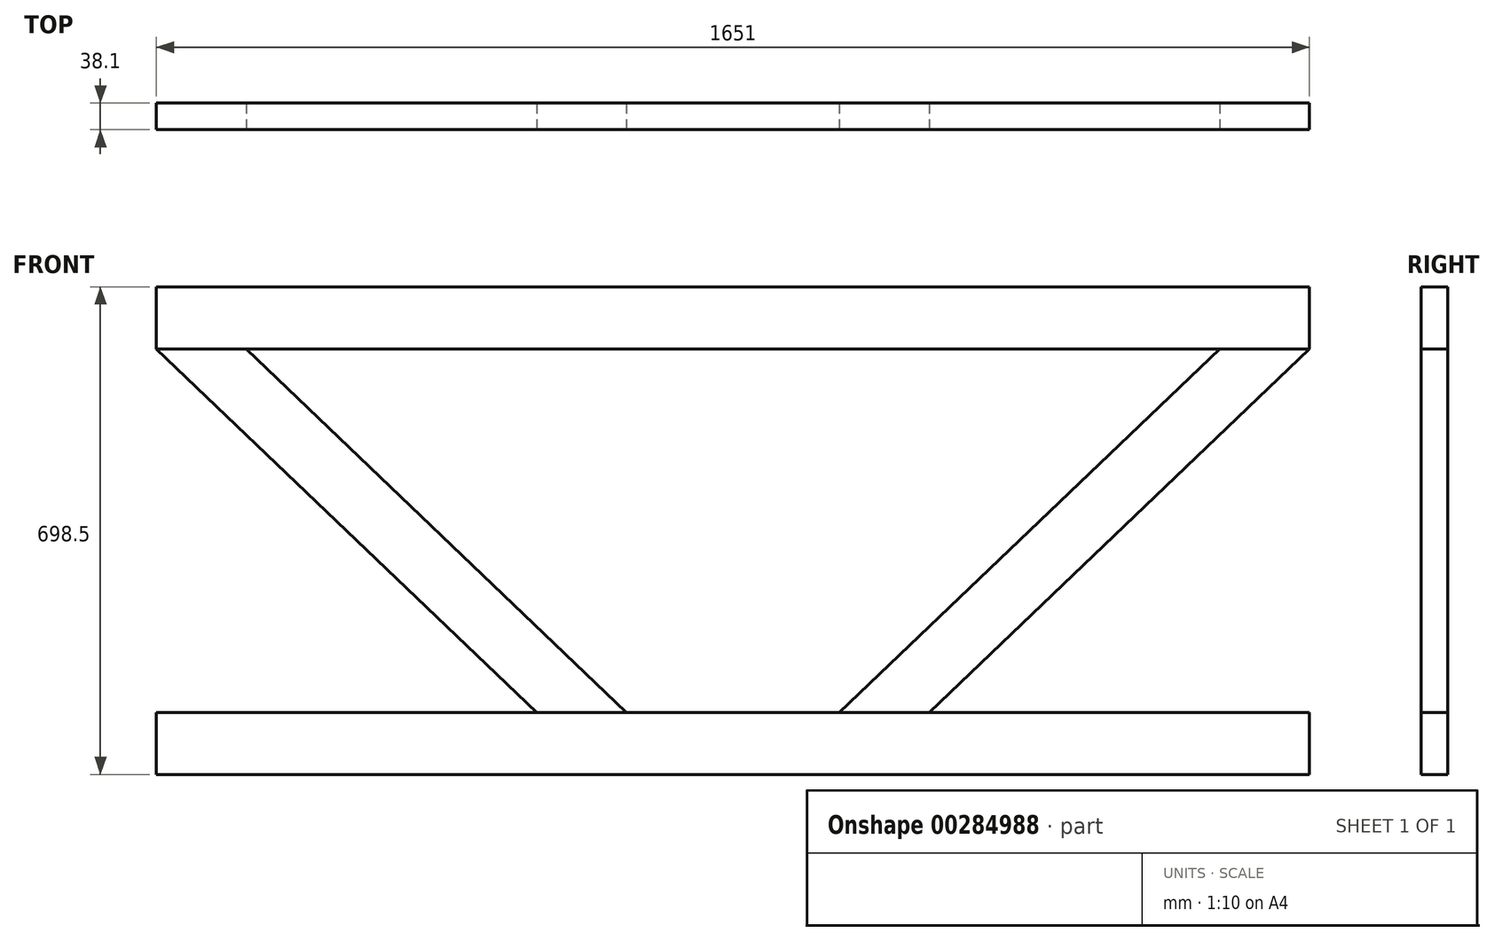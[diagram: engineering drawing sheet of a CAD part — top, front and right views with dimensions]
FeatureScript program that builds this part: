
annotation { "Feature Type Name" : "Feature", "Feature Type Description" : "" }
export const myFeature = defineFeature(function(context is Context, id is Id, definition is map)
    precondition{}
    {
        {
            var Q0;
            Q0=qCreatedBy(makeId("Front.planeOp"),FACE);
            var sketch = newSketch(context, id + "F0", { "sketchPlane" : qUnion([Q0])});
            skLineSegment(sketch, "E0.bottom", {"start": v(0, 0) * mm, "end": v(1651, 0) * mm});
            skLineSegment(sketch, "E0.top", {"start": v(0, 88.9) * mm, "end": v(1651, 88.9) * mm});
            skLineSegment(sketch, "E0.left", {"start": v(0, 0) * mm, "end": v(0, 88.9) * mm});
            skLineSegment(sketch, "E0.right", {"start": v(1651, 0) * mm, "end": v(1651, 88.9) * mm});
            skSolve(sketch);
        }
        {
            var Q0;
            Q0=makeQuery(id+"F0.imprint","IMPRINT",FACE,{"disambiguationData":[TD([[makeQuery(id+"F0.imprint","IMPRINT",EDGE,{"derivedFrom":sQuery(id+"F0.wireOp",EDGE,"E0.bottom")}),1.0]])]});
            extrude(context, id + "F1", {"entities" : qUnion([Q0]), "endBound" : BoundingType.SYMMETRIC, "depth" : 38.1 * mm});
        }
        {
            var Q0;
            Q0=qCreatedBy(makeId("Top.planeOp"),FACE);
            cPlane(context, id + "F2", {"entities" : qUnion([Q0]), "cplaneType" : CPlaneType.OFFSET, "offset" : 349.25 * mm, "width" : 152.4 * mm, "height" : 152.4 * mm});
        }
        {
            var Q0;
            Q0=makeQuery(id+"F1.opExtrude","SWEPT_BODY",BODY,{"disambiguationData":[OSD([sQuery(id+"F0.wireOp",EDGE,"E0.bottom"),sQuery(id+"F0.wireOp",EDGE,"E0.top"),sQuery(id+"F0.wireOp",EDGE,"E0.left"),sQuery(id+"F0.wireOp",EDGE,"E0.right")])]});
            var Q1;
            Q1=qCreatedBy(id+"F2.planeOp",FACE);
            mirror(context, id + "F3", {"entities" : qUnion([Q0]), "mirrorPlane" : qUnion([Q1])});
        }
        {
            var Q0;
            Q0=makeQuery(id+"F3.opPattern","COPY",FACE,{"derivedFrom":makeQuery(id+"F1.opExtrude","CAP_FACE",FACE,{"disambiguationData":[OSD([sQuery(id+"F0.wireOp",EDGE,"E0.bottom"),sQuery(id+"F0.wireOp",EDGE,"E0.top"),sQuery(id+"F0.wireOp",EDGE,"E0.left"),sQuery(id+"F0.wireOp",EDGE,"E0.right")])],"isStart":false}),"instanceName":"1"});
            var sketch = newSketch(context, id + "F4", { "sketchPlane" : qUnion([Q0])});
            skSolve(sketch);
        }
        {
            var Q0;
            Q0=makeQuery(id+"F4.imprint","IMPRINT",FACE,{"disambiguationData":[TD([[makeQuery(id+"F4.imprint","IMPRINT",EDGE,{"derivedFrom":makeQuery(id+"F3.opPattern","COPY",EDGE,{"derivedFrom":makeQuery(id+"F1.opExtrude","CAP_EDGE",EDGE,{"disambiguationData":[OSD([sQuery(id+"F0.wireOp",EDGE,"E0.bottom")])],"isStart":false}),"instanceName":"1"})}),-1.0]])]});
            var sketch = newSketch(context, id + "F5", { "sketchPlane" : qUnion([Q0])});
            skLineSegment(sketch, "E1", {"start": v(128.63, 609.6) * mm, "end": v(673.1, 88.9) * mm});
            skLineSegment(sketch, "E2", {"start": v(0, 609.6) * mm, "end": v(544.47, 88.9) * mm});
            skLineSegment(sketch, "E3", {"start": v(0, 609.6) * mm, "end": v(128.63, 609.6) * mm});
            skLineSegment(sketch, "E4", {"start": v(673.1, 88.9) * mm, "end": v(544.47, 88.9) * mm});
            skSolve(sketch);
        }
        {
            var Q0;
            Q0=makeQuery(id+"F5.imprint","IMPRINT",FACE,{"disambiguationData":[TD([[makeQuery(id+"F5.imprint","IMPRINT",EDGE,{"derivedFrom":sQuery(id+"F5.wireOp",EDGE,"E1")}),-1.0]])]});
            extrude(context, id + "F6", {"entities" : qUnion([Q0]), "oppositeDirection" : true, "depth" : 38.1 * mm});
        }
        {
            var Q0;
            Q0=qCreatedBy(makeId("Right.planeOp"),FACE);
            cPlane(context, id + "F7", {"entities" : qUnion([Q0]), "cplaneType" : CPlaneType.OFFSET, "offset" : 825.5 * mm, "width" : 152.4 * mm, "height" : 152.4 * mm});
        }
        {
            var Q0;
            Q0=makeQuery(id+"F6.opExtrude","SWEPT_BODY",BODY,{"disambiguationData":[OSD([sQuery(id+"F5.wireOp",EDGE,"E1"),sQuery(id+"F5.wireOp",EDGE,"E2"),sQuery(id+"F5.wireOp",EDGE,"E3"),sQuery(id+"F5.wireOp",EDGE,"E4")])]});
            var Q1;
            Q1=qCreatedBy(id+"F7.planeOp",FACE);
            mirror(context, id + "F8", {"entities" : qUnion([Q0]), "mirrorPlane" : qUnion([Q1])});
        }
    });
